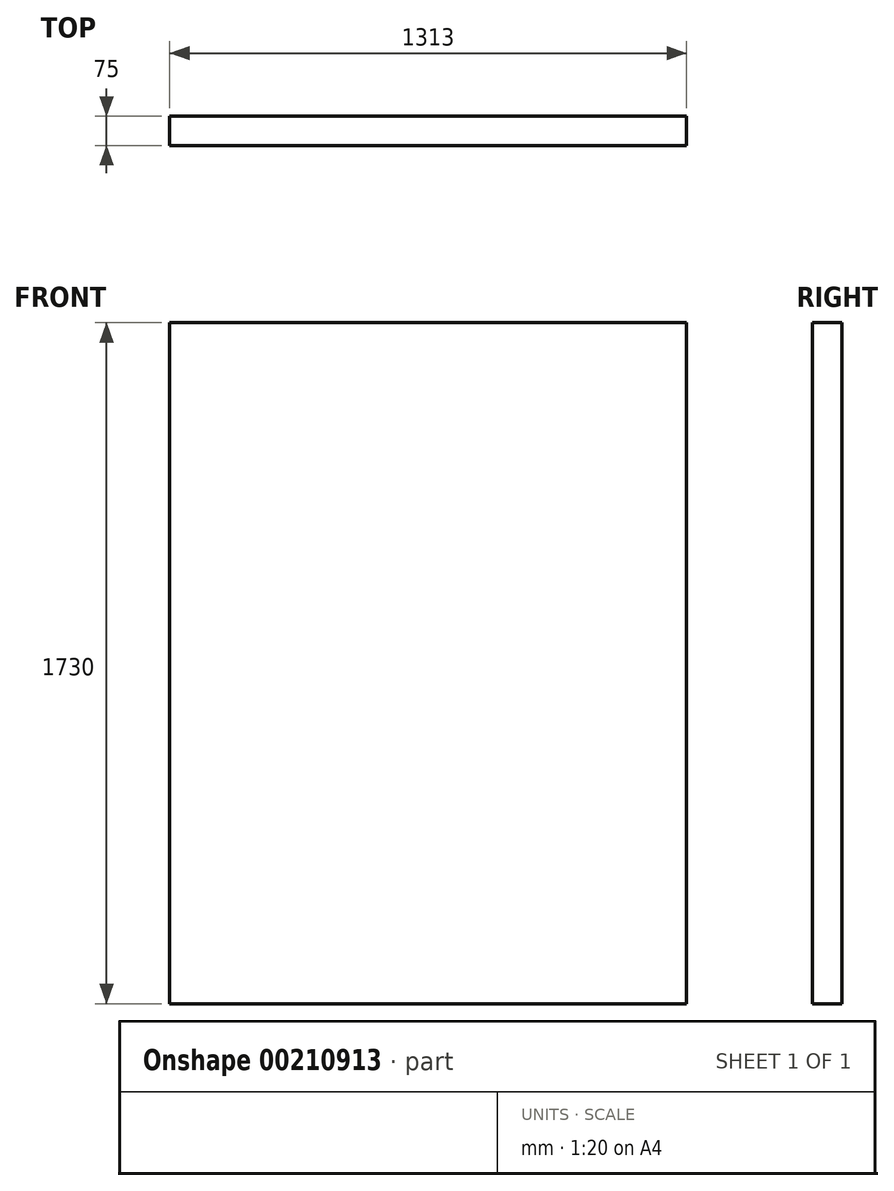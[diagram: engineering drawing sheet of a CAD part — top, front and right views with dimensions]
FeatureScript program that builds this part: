
annotation { "Feature Type Name" : "Feature", "Feature Type Description" : "" }
export const myFeature = defineFeature(function(context is Context, id is Id, definition is map)
    precondition{}
    {
        {
            var Q0;
            Q0=qCreatedBy(makeId("Front.planeOp"),FACE);
            var sketch = newSketch(context, id + "F0", { "sketchPlane" : qUnion([Q0])});
            skLineSegment(sketch, "E0.bottom", {"start": v(0, 0) * mm, "end": v(1313, 0) * mm});
            skLineSegment(sketch, "E0.right", {"start": v(1313, 0) * mm, "end": v(1313, 1730) * mm});
            skLineSegment(sketch, "E1", {"start": v(0, 1730) * mm, "end": v(1313, 1730) * mm});
            skLineSegment(sketch, "E2", {"start": v(0, 0) * mm, "end": v(0, 1730) * mm});
            skSolve(sketch);
        }
        {
            var Q0;
            Q0=makeQuery(id+"F0.imprint","IMPRINT",FACE,{"disambiguationData":[TD([[makeQuery(id+"F0.imprint","IMPRINT",EDGE,{"derivedFrom":sQuery(id+"F0.wireOp",EDGE,"E0.bottom")}),1.0]])]});
            extrude(context, id + "F1", {"entities" : qUnion([Q0]), "depth" : 75 * mm});
        }
    });
